# Revit family: Sanitary_Wash-basins_Hansgrohe_60104XXX-GladeLake-S-Half-pedestal-for-w_31
name_source: partatom
category: Plumbing Fixtures
revit_build: Autodesk Revit 2018 (Build: 20170223_1515(x64)
units: mm (PartAtom-declared; Revit-internal decimal feet)

## family parameters
Always vertical = No
Cut with Voids When Loaded = No
OmniClass Number = 23.31.13.17
OmniClass Title = Sink Components
Part Type = Normal
Room Calculation Point = No
Round Connector Dimension = Use Diameter
Shared = No
Work Plane-Based = Yes

## types (1)
- 450 White
    Always visible = Yes
    BIMobject category = Wash basins
    Default Elevation = 1219.2 mm  [stored 4 ft]
    Description = GladeLake S Half pedestal for washbasin
    Design country = Germany
    EAN code = 4059625477878
    Edition number = 1
    GTIN code = https://4059625477878
    IFC Classification = Furnishing Element
    Manufacturer = Hansgrohe
    Manufacturer country = Germany
    Manufacturer name = hansgrohe
    Material 1 = Hansgrohe - Ceramic - 450 White
    Model = 60104XXX
    OmniClass Code = 23-31 13 17
    OmniClass Description = Sink Components
    Product Guid = cd7fc170-872e-4c08-845d-034f4a639292
    Product SKU = 60104XXX
    Product data url = https://bimobject.com
    Product family = GladeLake S
    Product group = half pedestals
    Product name = 60104XXX GladeLake S Half pedestal for washbasin
    Product url = https://pro.hansgrohe.com
    QR code = https://bimobject.com
    URL = https://www.hansgrohe.com
    Uniclass 2015 Code = Pr_40_20_96_63
    Uniclass 2015 Name = Pedestal wash basins
    Weight Net (Kg) = 7,2

note: [stored X ft] marks values corroborated as IEEE doubles in the binary element streams (Revit-internal decimal feet)

## geometry (parser evidence)
native form markers: Sweep x2
no freeform markers — native parametric forms only
